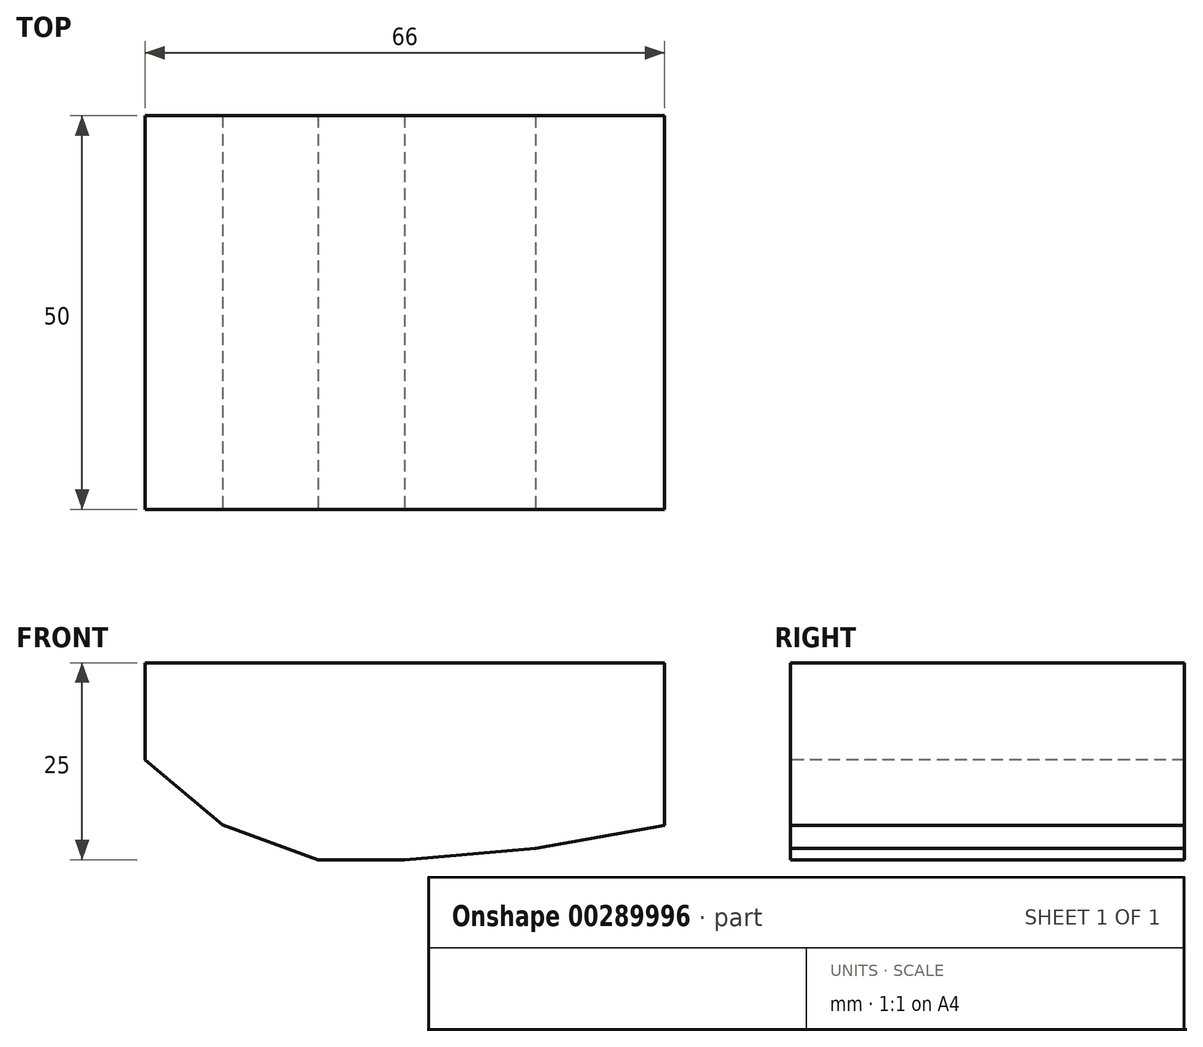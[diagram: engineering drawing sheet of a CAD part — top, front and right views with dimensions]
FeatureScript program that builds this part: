
annotation { "Feature Type Name" : "Feature", "Feature Type Description" : "" }
export const myFeature = defineFeature(function(context is Context, id is Id, definition is map)
    precondition{}
    {
        {
            var Q0;
            Q0=qCreatedBy(makeId("Top.planeOp"),FACE);
            var sketch = newSketch(context, id + "F0", { "sketchPlane" : qUnion([Q0])});
            skLineSegment(sketch, "E0.bottom", {"start": v(-33, 25) * mm, "end": v(33, 25) * mm});
            skLineSegment(sketch, "E0.top", {"start": v(-33, -25) * mm, "end": v(33, -25) * mm});
            skLineSegment(sketch, "E0.left", {"start": v(-33, 25) * mm, "end": v(-33, -25) * mm});
            skLineSegment(sketch, "E0.right", {"start": v(33, 25) * mm, "end": v(33, -25) * mm});
            skPoint(sketch, "E0.middle", {"position": v(0, 0) * mm});
            skSolve(sketch);
        }
        {
            var Q0;
            Q0=makeQuery(id+"F0.imprint","IMPRINT",FACE,{"disambiguationData":[TD([[makeQuery(id+"F0.imprint","IMPRINT",EDGE,{"derivedFrom":sQuery(id+"F0.wireOp",EDGE,"E0.bottom")}),-1.0]])]});
            extrude(context, id + "F1", {"entities" : qUnion([Q0]), "depth" : 25 * mm});
        }
        {
            var Q0;
            Q0=makeQuery(id+"F1.opExtrude","SWEPT_FACE",FACE,{"disambiguationData":[OSD([sQuery(id+"F0.wireOp",EDGE,"E0.top")])]});
            var sketch = newSketch(context, id + "F2", { "sketchPlane" : qUnion([Q0])});
            skLineSegment(sketch, "E1", {"start": v(-11, 0) * mm, "end": v(-23.12, 4.41) * mm});
            skLineSegment(sketch, "E2", {"start": v(-23.12, 4.41) * mm, "end": v(-33, 12.7) * mm});
            skLineSegment(sketch, "E3", {"start": v(0, 0) * mm, "end": v(16.6, 1.45) * mm});
            skLineSegment(sketch, "E4", {"start": v(16.6, 1.45) * mm, "end": v(33, 4.34) * mm});
            skSolve(sketch);
        }
        {
            var Q0;
            {var subQ0=sQuery(id+"F2.wireOp",EDGE,"E1");Q0=makeQuery(id+"F2.imprint","IMPRINT",FACE,{"disambiguationData":[TD([[makeQuery(id+"F2.imprint","IMPRINT",EDGE,{"derivedFrom":subQ0}),1.0]])]});}
            var Q1;
            {var subQ0=sQuery(id+"F2.wireOp",EDGE,"E3");Q1=makeQuery(id+"F2.imprint","IMPRINT",FACE,{"disambiguationData":[TD([[makeQuery(id+"F2.imprint","IMPRINT",EDGE,{"derivedFrom":subQ0}),-1.0]])]});}
            extrude(context, id + "F3", {"entities" : qUnion([Q0, Q1]), "operationType" : NewBodyOperationType.REMOVE, "oppositeDirection" : true, "depth" : 50 * mm});
        }
    });
